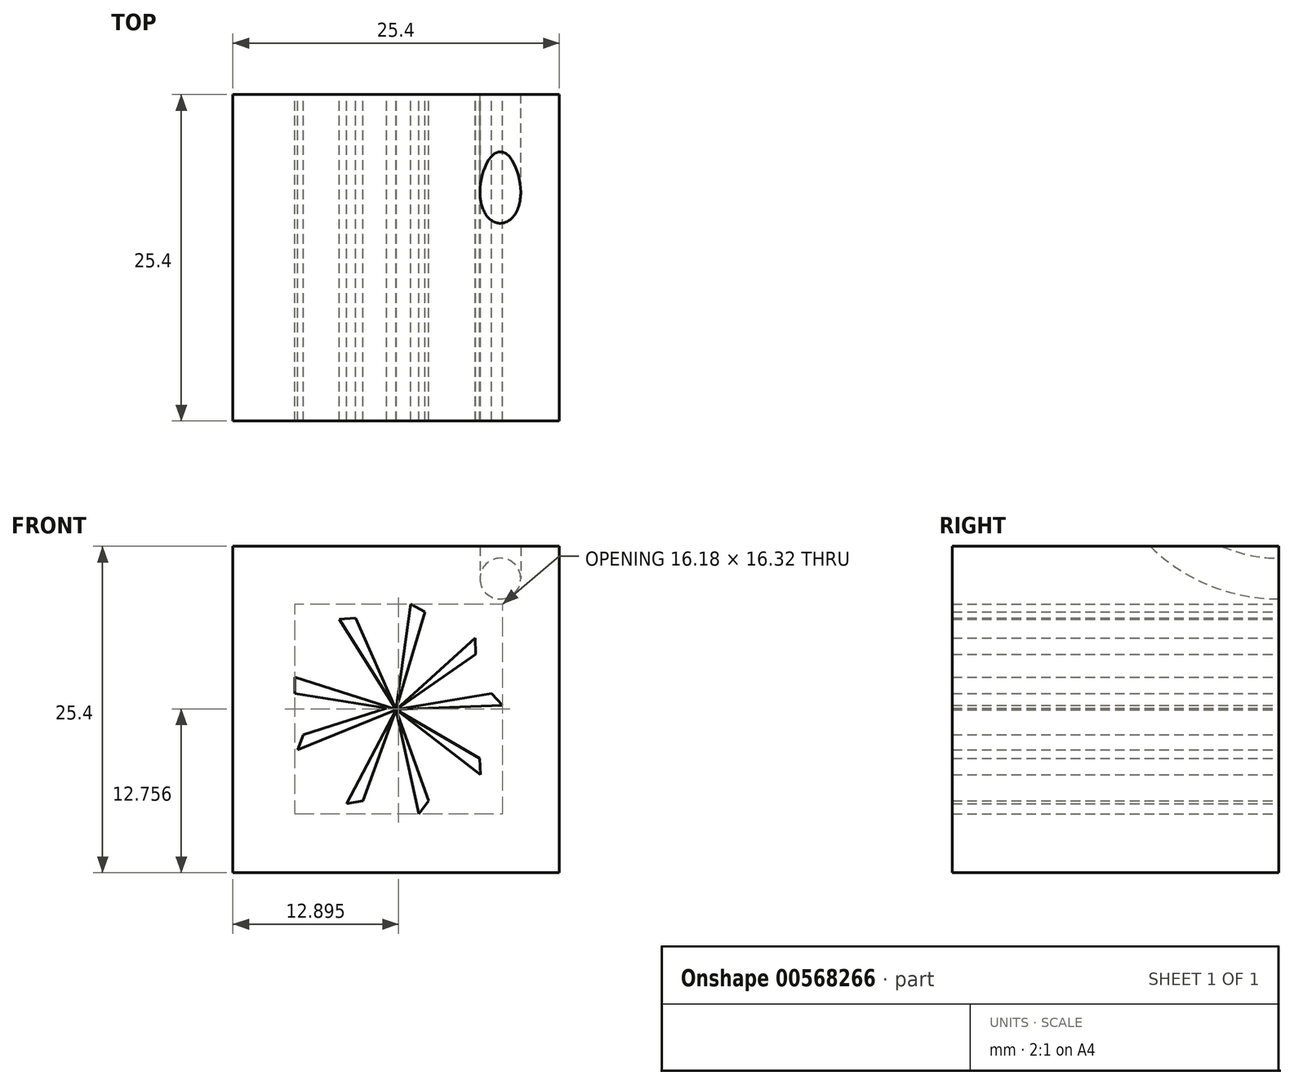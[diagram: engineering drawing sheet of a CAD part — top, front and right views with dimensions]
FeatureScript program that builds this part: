
annotation { "Feature Type Name" : "Feature", "Feature Type Description" : "" }
export const myFeature = defineFeature(function(context is Context, id is Id, definition is map)
    precondition{}
    {
        {
            var Q0;
            Q0=qCreatedBy(makeId("Front.planeOp"),FACE);
            var sketch = newSketch(context, id + "F0", { "sketchPlane" : qUnion([Q0])});
            skLineSegment(sketch, "E0", {"start": v(0, 0) * mm, "end": v(0, 25.4) * mm});
            skLineSegment(sketch, "E1", {"start": v(0, 25.4) * mm, "end": v(25.4, 25.4) * mm});
            skLineSegment(sketch, "E2", {"start": v(25.4, 25.4) * mm, "end": v(25.4, 0) * mm});
            skLineSegment(sketch, "E3", {"start": v(25.4, 0) * mm, "end": v(0, 0) * mm});
            skLineSegment(sketch, "E4", {"start": v(12.71, 12.71) * mm, "end": v(18.84, 18.27) * mm});
            skPoint(sketch, "E4.startSnap0", {"position": v(12.7, 25.4) * mm});
            skPoint(sketch, "E4.startSnap1", {"position": v(25.4, 12.7) * mm});
            skLineSegment(sketch, "E5.1.0", {"start": v(12.7, 12.72) * mm, "end": v(13.82, 20.91) * mm});
            skLineSegment(sketch, "E5.2.0", {"start": v(12.7, 12.72) * mm, "end": v(12.52, 13) * mm});
            skLineSegment(sketch, "E5.3.0", {"start": v(12.68, 12.7) * mm, "end": v(4.8, 15.23) * mm});
            skLineSegment(sketch, "E5.4.0", {"start": v(12.68, 12.7) * mm, "end": v(5.03, 9.57) * mm});
            skLineSegment(sketch, "E5.5.0", {"start": v(12.7, 12.68) * mm, "end": v(8.84, 5.37) * mm});
            skLineSegment(sketch, "E5.6.0", {"start": v(12.7, 12.68) * mm, "end": v(14.45, 4.6) * mm});
            skLineSegment(sketch, "E5.7.0", {"start": v(12.71, 12.69) * mm, "end": v(19.25, 7.62) * mm});
            skLineSegment(sketch, "E5.8.0", {"start": v(12.72, 12.7) * mm, "end": v(20.98, 13.02) * mm});
            skPoint(sketch, "E5.center", {"position": v(12.7, 12.7) * mm});
            skLineSegment(sketch, "E6", {"start": v(13.82, 20.91) * mm, "end": v(14.94, 20.31) * mm});
            skLineSegment(sketch, "E7", {"start": v(14.94, 20.31) * mm, "end": v(12.7, 12.72) * mm});
            skLineSegment(sketch, "E8", {"start": v(18.84, 18.27) * mm, "end": v(18.89, 17) * mm});
            skLineSegment(sketch, "E9", {"start": v(18.89, 17) * mm, "end": v(12.72, 12.71) * mm});
            skLineSegment(sketch, "E10", {"start": v(8.28, 19.71) * mm, "end": v(9.54, 19.84) * mm});
            skLineSegment(sketch, "E11", {"start": v(4.8, 15.23) * mm, "end": v(4.8, 13.96) * mm});
            skLineSegment(sketch, "E12", {"start": v(4.8, 13.96) * mm, "end": v(12.68, 12.7) * mm});
            skLineSegment(sketch, "E13", {"start": v(20.98, 13.02) * mm, "end": v(20.13, 13.96) * mm});
            skLineSegment(sketch, "E14", {"start": v(20.13, 13.96) * mm, "end": v(12.72, 12.7) * mm});
            skLineSegment(sketch, "E15", {"start": v(5.03, 9.57) * mm, "end": v(5.5, 10.75) * mm});
            skLineSegment(sketch, "E16", {"start": v(5.5, 10.75) * mm, "end": v(11.97, 12.82) * mm});
            skLineSegment(sketch, "E17", {"start": v(19.25, 7.62) * mm, "end": v(19.2, 8.9) * mm});
            skLineSegment(sketch, "E18", {"start": v(19.2, 8.9) * mm, "end": v(12.72, 12.7) * mm});
            skLineSegment(sketch, "E19", {"start": v(14.45, 4.6) * mm, "end": v(15.23, 5.6) * mm});
            skLineSegment(sketch, "E20", {"start": v(15.23, 5.6) * mm, "end": v(12.7, 12.68) * mm});
            skLineSegment(sketch, "E21", {"start": v(8.84, 5.37) * mm, "end": v(10.1, 5.6) * mm});
            skLineSegment(sketch, "E22", {"start": v(10.1, 5.6) * mm, "end": v(12.7, 12.68) * mm});
            skLineSegment(sketch, "E23", {"start": v(9.54, 19.84) * mm, "end": v(12.7, 12.72) * mm});
            skLineSegment(sketch, "E24", {"start": v(8.28, 19.71) * mm, "end": v(12.7, 12.72) * mm});
            skCircle(sketch, "E25", {"center": v(12.7, 12.7) * mm, "radius": 0.02 * mm});
            skSolve(sketch);
        }
        {
            var Q0;
            Q0=makeQuery(id+"F0.imprint","IMPRINT",FACE,{"disambiguationData":[TD([[makeQuery(id+"F0.imprint","IMPRINT",EDGE,{"derivedFrom":sQuery(id+"F0.wireOp",EDGE,"E0")}),-1.0]])]});
            extrude(context, id + "F1", {"entities" : qUnion([Q0]), "depth" : 25.4 * mm, "offsetDistance" : 25.4 * mm});
        }
        {
            var Q0;
            Q0=qCreatedBy(makeId("Front.planeOp"),FACE);
            var sketch = newSketch(context, id + "F2", { "sketchPlane" : qUnion([Q0])});
            skLineSegment(sketch, "E26", {"start": v(25.4, 25.4) * mm, "end": v(0, 25.4) * mm});
            skLineSegment(sketch, "E27", {"start": v(0, 25.4) * mm, "end": v(0, 0) * mm});
            skLineSegment(sketch, "E28", {"start": v(0.1, -0.25) * mm, "end": v(25.08, 0) * mm});
            skLineSegment(sketch, "E29", {"start": v(25.08, 0) * mm, "end": v(25.4, 25.4) * mm});
            skCircle(sketch, "E30", {"center": v(20.8, 22.89) * mm, "radius": 1.59 * mm});
            skLineSegment(sketch, "E31", {"start": v(0, 35.59) * mm, "end": v(28.76, 35.59) * mm});
            skSolve(sketch);
        }
        {
            var Q0;
            Q0=makeQuery(id+"F2.imprint","IMPRINT",FACE,{"disambiguationData":[TD([[makeQuery(id+"F2.imprint","IMPRINT",EDGE,{"derivedFrom":sQuery(id+"F2.wireOp",EDGE,"E30")}),1.0]])]});
            var Q1;
            Q1=sQuery(id+"F2.wireOp",EDGE,"E31");
            revolve(context, id + "F3", {"operationType" : NewBodyOperationType.REMOVE, "entities" : qUnion([Q0]), "axis" : qUnion([Q1]), "revolveType" : RevolveType.FULL, "oppositeDirection" : true});
        }
    });
